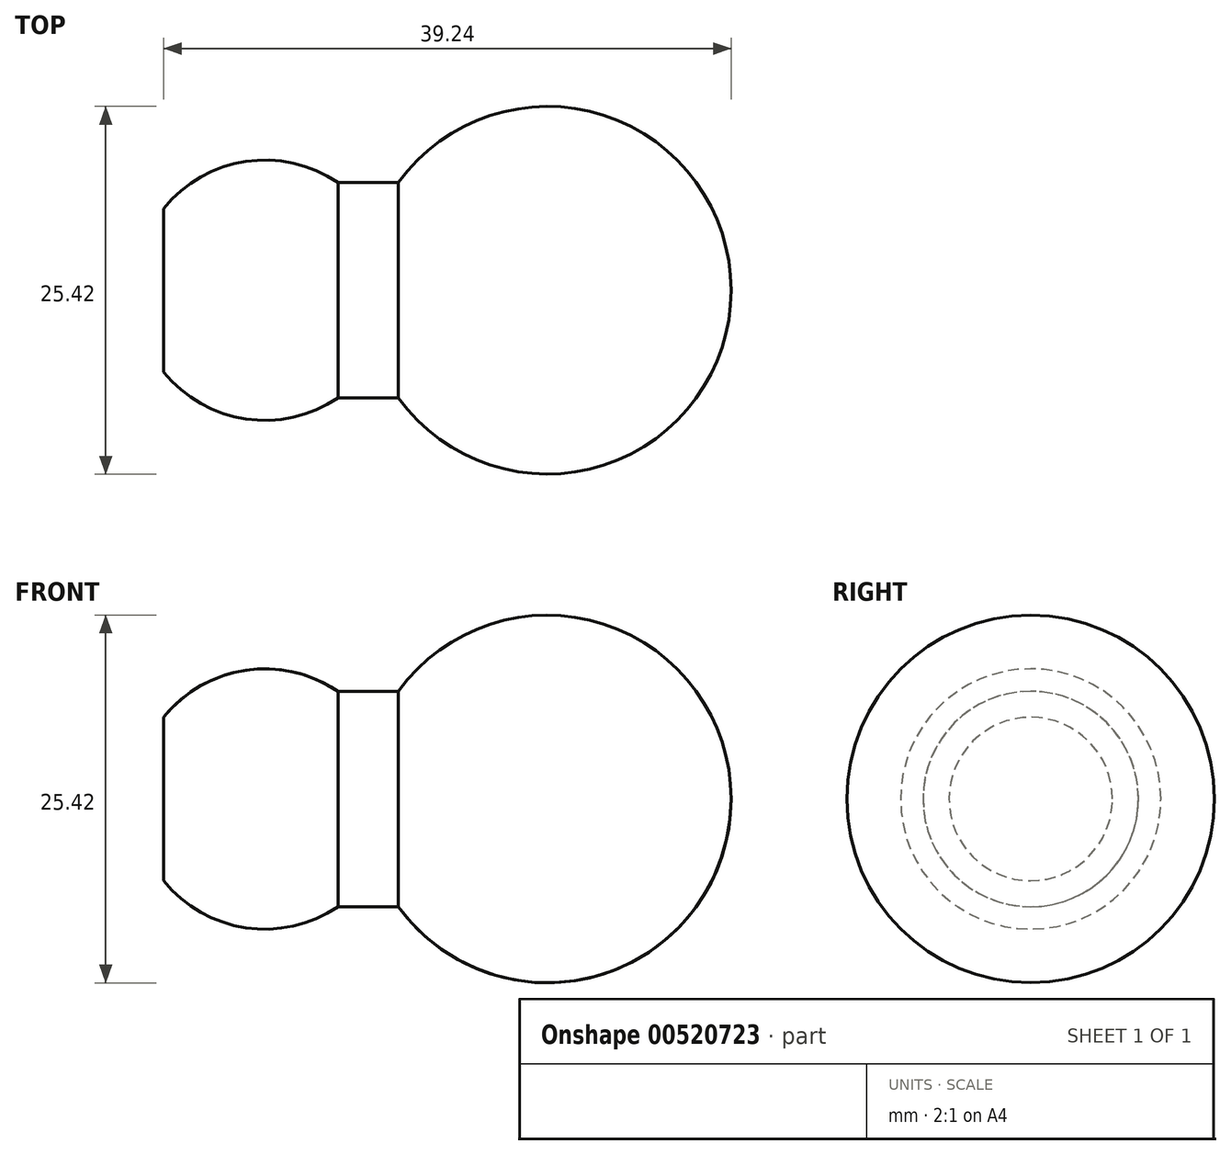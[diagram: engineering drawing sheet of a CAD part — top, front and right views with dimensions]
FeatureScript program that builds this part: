
annotation { "Feature Type Name" : "Feature", "Feature Type Description" : "" }
export const myFeature = defineFeature(function(context is Context, id is Id, definition is map)
    precondition{}
    {
        {
            var Q0;
            Q0=qCreatedBy(makeId("Front.planeOp"),FACE);
            var sketch = newSketch(context, id + "F0", { "sketchPlane" : qUnion([Q0])});
            skArc(sketch, "E0", {"start": v(44.5, 0) * mm, "mid": v(35.7, 12.09) * mm, "end": v(21.5, 7.45) * mm});
            skLineSegment(sketch, "E1", {"start": v(12.26, 0) * mm, "end": v(17.26, 0) * mm});
            skLineSegment(sketch, "E2.bottom", {"start": v(17.26, 0) * mm, "end": v(29.88, 0) * mm});
            skLineSegment(sketch, "E2.top", {"start": v(17.26, 7.45) * mm, "end": v(29.88, 7.45) * mm});
            skLineSegment(sketch, "E3", {"start": v(12.26, 0) * mm, "end": v(5.26, 0) * mm});
            skLineSegment(sketch, "E4.left", {"start": v(5.26, 0) * mm, "end": v(5.26, 5.7) * mm});
            skLineSegment(sketch, "E5", {"start": v(5.26, 0) * mm, "end": v(44.5, 0) * mm});
            skArc(sketch, "E6.trimOffspring", {"start": v(17.31, 7.45) * mm, "mid": v(10.93, 8.9) * mm, "end": v(5.26, 5.65) * mm});
            skSolve(sketch);
        }
        {
            var Q0;
            {var subQ1=sQuery(id+"F0.wireOp",EDGE,"E0");Q0=makeQuery(id+"F0.imprint","IMPRINT",FACE,{"disambiguationData":[TD([[makeQuery(id+"F0.imprint","IMPRINT",EDGE,{"derivedFrom":subQ1}),1.0]])]});}
            var Q1;
            Q1=sQuery(id+"F0.wireOp",EDGE,"E5");
            revolve(context, id + "F1", {"entities" : qUnion([Q0]), "axis" : qUnion([Q1]), "revolveType" : RevolveType.FULL});
        }
    });
